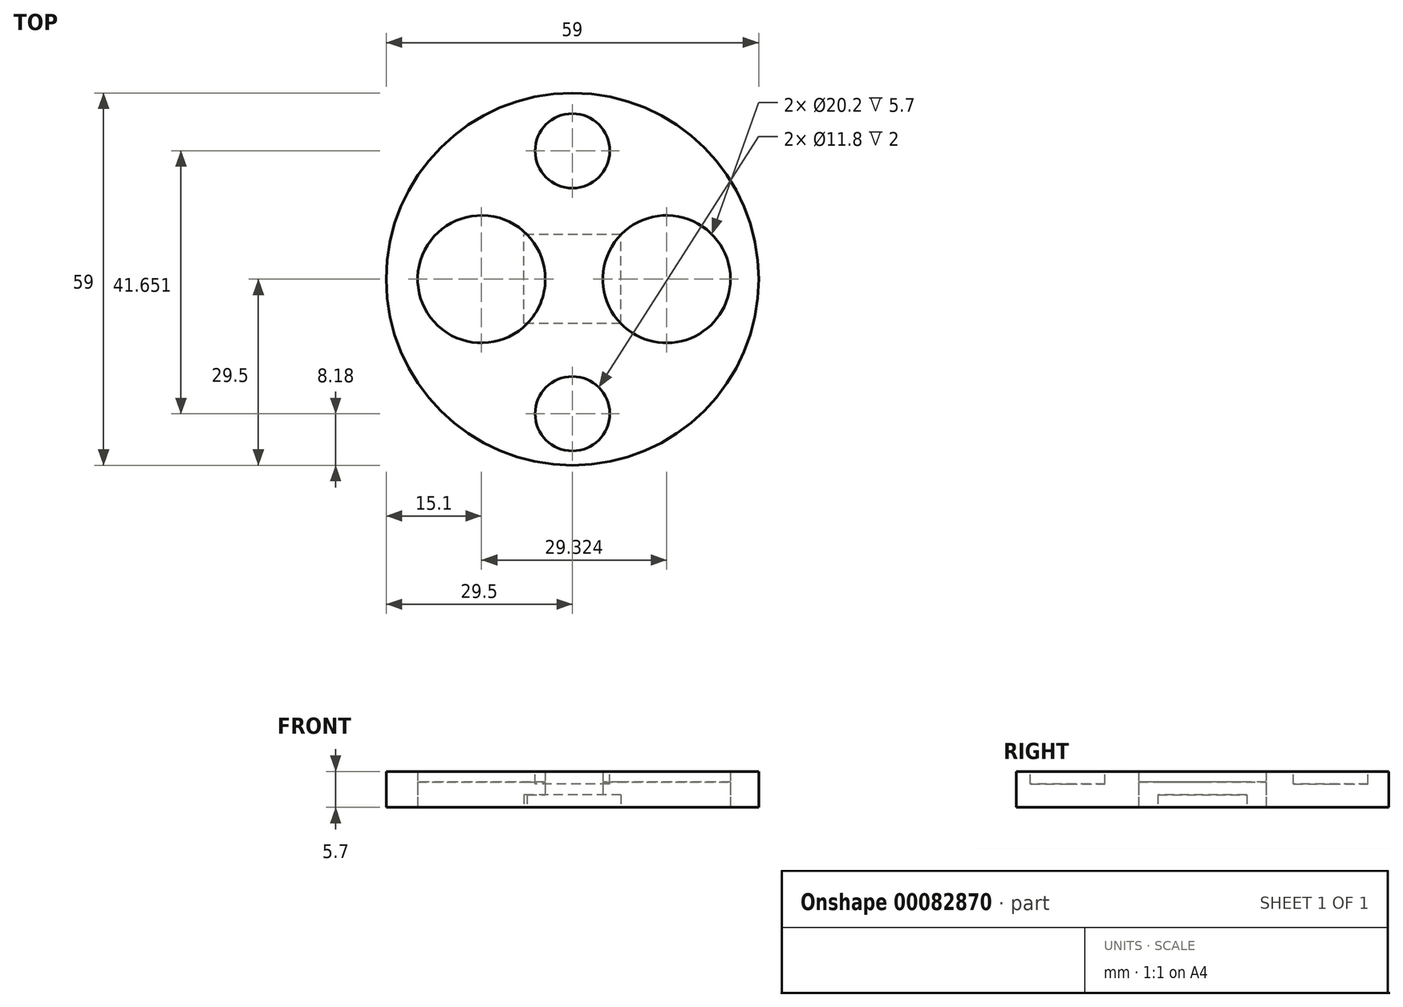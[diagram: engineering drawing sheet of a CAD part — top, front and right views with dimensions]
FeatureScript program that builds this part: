
annotation { "Feature Type Name" : "Feature", "Feature Type Description" : "" }
export const myFeature = defineFeature(function(context is Context, id is Id, definition is map)
    precondition{}
    {
        {
            var Q0;
            Q0=qCreatedBy(makeId("Top.planeOp"),FACE);
            var sketch = newSketch(context, id + "F0", { "sketchPlane" : qUnion([Q0])});
            skCircle(sketch, "E0", {"center": v(0, 0) * mm, "radius": 29.5 * mm});
            skCircle(sketch, "E1", {"center": v(-14.4, 0) * mm, "radius": 10.1 * mm});
            skCircle(sketch, "E2", {"center": v(14.92, 0) * mm, "radius": 10.1 * mm});
            skSolve(sketch);
        }
        {
            var Q0;
            Q0=makeQuery(id+"F0.imprint","IMPRINT",FACE,{"disambiguationData":[TD([[makeQuery(id+"F0.imprint","IMPRINT",EDGE,{"derivedFrom":sQuery(id+"F0.wireOp",EDGE,"E1")}),1.0]])]});
            var Q1;
            Q1=makeQuery(id+"F0.imprint","IMPRINT",FACE,{"disambiguationData":[TD([[makeQuery(id+"F0.imprint","IMPRINT",EDGE,{"derivedFrom":sQuery(id+"F0.wireOp",EDGE,"E2")}),1.0]])]});
            extrude(context, id + "F1", {"entities" : qUnion([Q0, Q1]), "depth" : 4 * mm});
        }
        {
            var Q0;
            Q0=qSketchRegion(id+"F0",true);
            extrude(context, id + "F2", {"entities" : qUnion([Q0]), "depth" : 5.7 * mm});
        }
        {
            var Q0;
            Q0=makeQuery(id+"F2.opExtrude","CAP_FACE",FACE,{"disambiguationData":[OSD([sQuery(id+"F0.wireOp",EDGE,"E0"),sQuery(id+"F0.wireOp",EDGE,"E1"),sQuery(id+"F0.wireOp",EDGE,"E2")])],"isStart":false});
            var sketch = newSketch(context, id + "F3", { "sketchPlane" : qUnion([Q0])});
            skCircle(sketch, "E3", {"center": v(0, 20.33) * mm, "radius": 5.9 * mm});
            skCircle(sketch, "E4", {"center": v(0, -21.32) * mm, "radius": 5.9 * mm});
            skSolve(sketch);
        }
        {
            var Q0;
            Q0=qSketchRegion(id+"F3",true);
            extrude(context, id + "F4", {"entities" : qUnion([Q0]), "operationType" : NewBodyOperationType.REMOVE, "oppositeDirection" : true, "depth" : 2 * mm});
        }
        {
            var Q0;
            Q0=makeQuery(id+"F2.opExtrude","CAP_FACE",FACE,{"disambiguationData":[OSD([sQuery(id+"F0.wireOp",EDGE,"E0"),sQuery(id+"F0.wireOp",EDGE,"E1"),sQuery(id+"F0.wireOp",EDGE,"E2")])],"isStart":true});
            var sketch = newSketch(context, id + "F5", { "sketchPlane" : qUnion([Q0])});
            skLineSegment(sketch, "E5.bottom", {"start": v(7.7, 7.05) * mm, "end": v(-7.7, 7.05) * mm});
            skLineSegment(sketch, "E5.top", {"start": v(7.7, -7.05) * mm, "end": v(-7.7, -7.05) * mm});
            skLineSegment(sketch, "E5.left", {"start": v(7.7, 7.05) * mm, "end": v(7.7, -7.05) * mm});
            skLineSegment(sketch, "E5.right", {"start": v(-7.7, 7.05) * mm, "end": v(-7.7, -7.05) * mm});
            skPoint(sketch, "E5.middle", {"position": v(0, 0) * mm});
            skSolve(sketch);
        }
        {
            var Q0;
            Q0=qSketchRegion(id+"F5",true);
            extrude(context, id + "F6", {"entities" : qUnion([Q0]), "operationType" : NewBodyOperationType.REMOVE, "oppositeDirection" : true, "depth" : 2 * mm});
        }
    });
